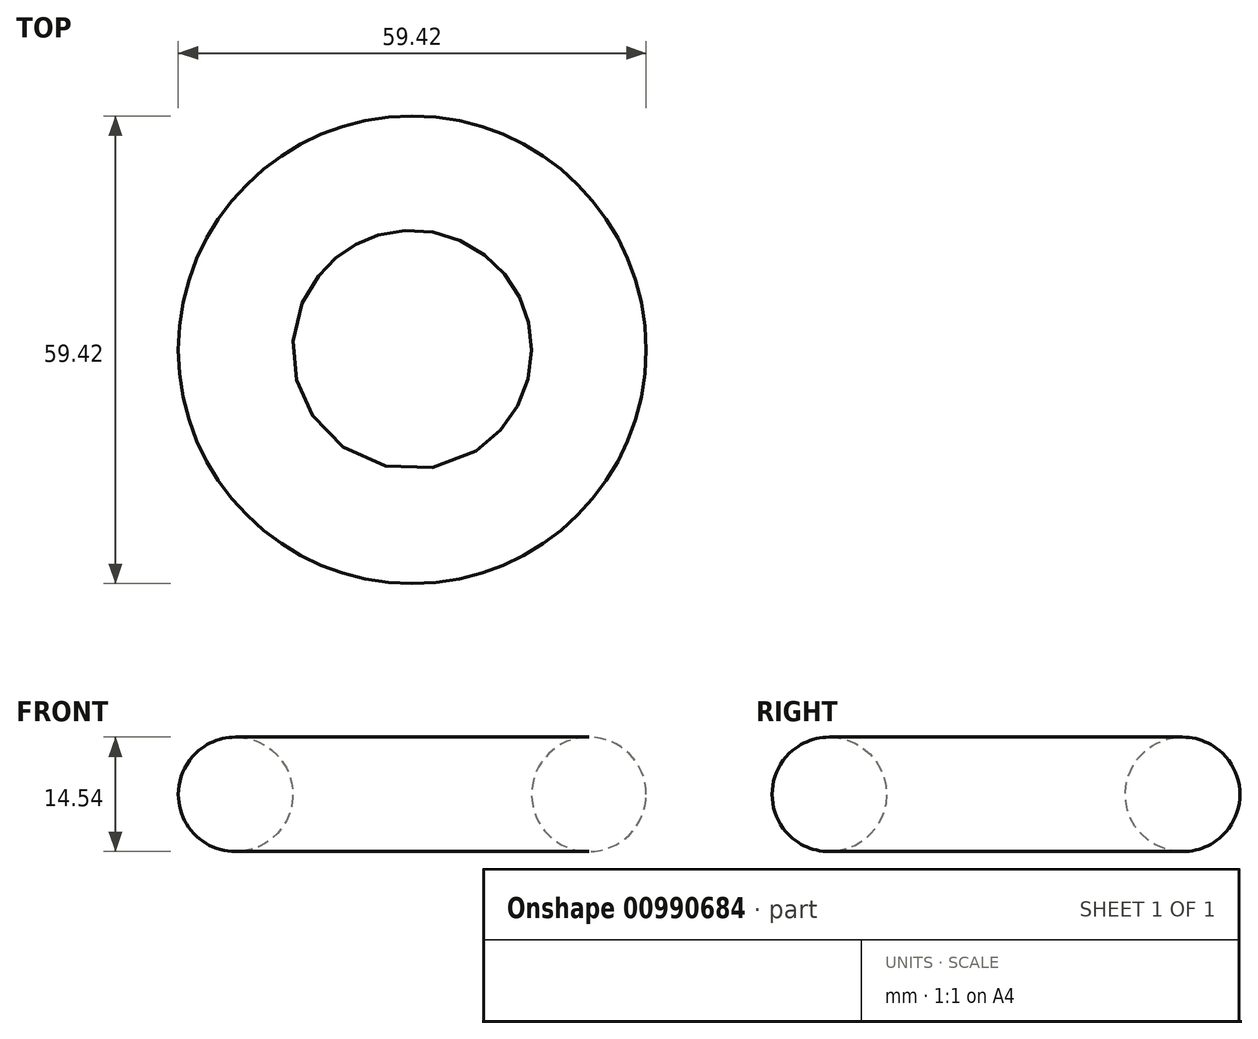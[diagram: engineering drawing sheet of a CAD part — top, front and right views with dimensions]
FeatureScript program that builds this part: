
annotation { "Feature Type Name" : "Feature", "Feature Type Description" : "" }
export const myFeature = defineFeature(function(context is Context, id is Id, definition is map)
    precondition{}
    {
        {
            var Q0;
            Q0=qCreatedBy(makeId("Front.planeOp"),FACE);
            var sketch = newSketch(context, id + "F0", { "sketchPlane" : qUnion([Q0])});
            skCircle(sketch, "E0", {"center": v(22.44, 0) * mm, "radius": 7.27 * mm});
            skLineSegment(sketch, "E1", {"start": v(0, 18.12) * mm, "end": v(0, -11.22) * mm, "construction": true});
            skSolve(sketch);
        }
        {
            var Q0;
            Q0=makeQuery(id+"F0.imprint","IMPRINT",FACE,{"disambiguationData":[TD([[makeQuery(id+"F0.imprint","IMPRINT",EDGE,{"derivedFrom":sQuery(id+"F0.wireOp",EDGE,"E0")}),1.0]])]});
            var Q1;
            Q1=sQuery(id+"F0.wireOp",EDGE,"E1");
            revolve(context, id + "F1", {"surfaceOperationType" : NewSurfaceOperationType.NEW, "entities" : qUnion([Q0]), "axis" : qUnion([Q1]), "revolveType" : RevolveType.FULL});
        }
    });
